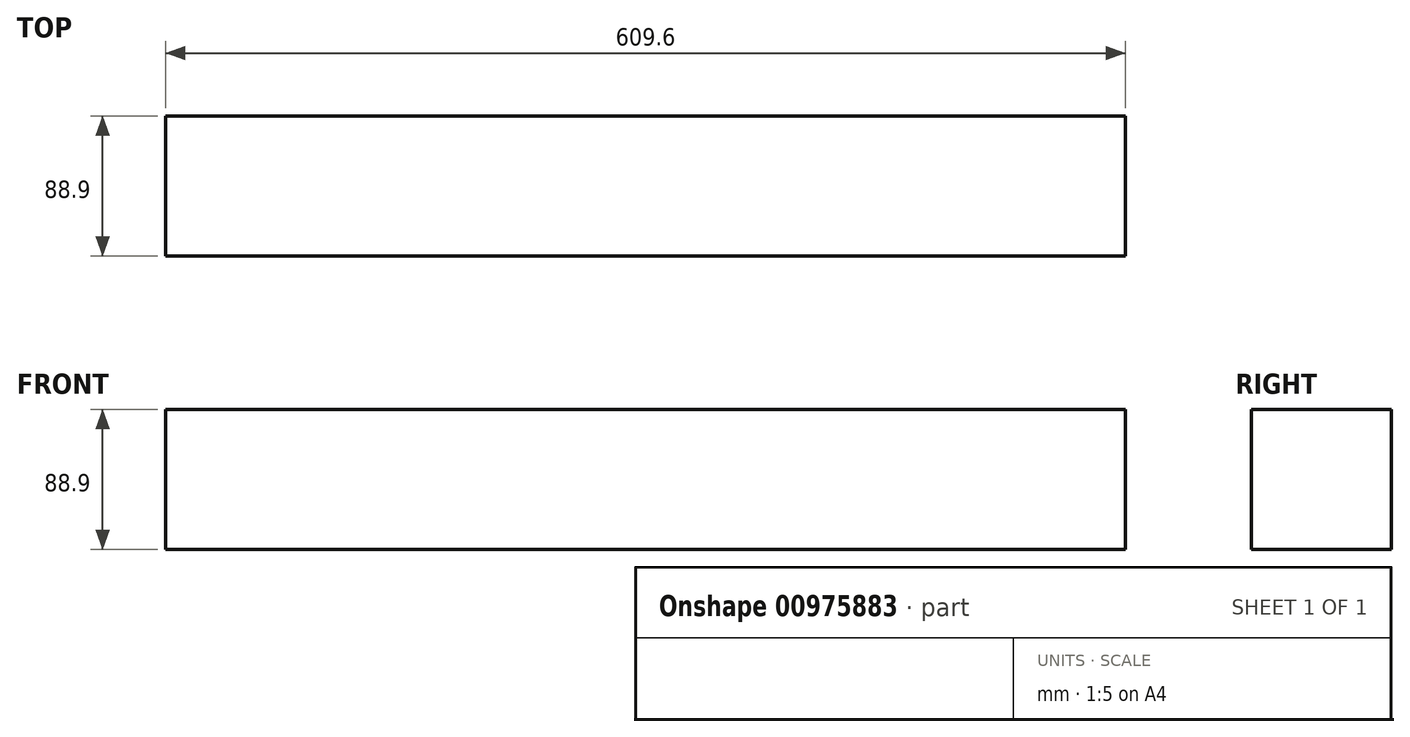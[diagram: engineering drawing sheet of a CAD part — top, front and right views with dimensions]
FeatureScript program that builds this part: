
annotation { "Feature Type Name" : "Feature", "Feature Type Description" : "" }
export const myFeature = defineFeature(function(context is Context, id is Id, definition is map)
    precondition{}
    {
        {
            var Q0;
            Q0=qCreatedBy(makeId("Right.planeOp"),FACE);
            var sketch = newSketch(context, id + "F0", { "sketchPlane" : qUnion([Q0])});
            skLineSegment(sketch, "E0.bottom", {"start": v(0, 0) * mm, "end": v(0, 0) * mm});
            skLineSegment(sketch, "E0.top", {"start": v(0, 0) * mm, "end": v(0, 0) * mm});
            skLineSegment(sketch, "E0.left", {"start": v(0, 0) * mm, "end": v(0, 0) * mm});
            skLineSegment(sketch, "E0.right", {"start": v(0, 0) * mm, "end": v(0, 0) * mm});
            skPoint(sketch, "E0.middle", {"position": v(0, 0) * mm});
            skLineSegment(sketch, "E1.bottom", {"start": v(44.45, 44.45) * mm, "end": v(-44.45, 44.45) * mm});
            skLineSegment(sketch, "E1.top", {"start": v(44.45, -44.45) * mm, "end": v(-44.45, -44.45) * mm});
            skLineSegment(sketch, "E1.left", {"start": v(44.45, 44.45) * mm, "end": v(44.45, -44.45) * mm});
            skLineSegment(sketch, "E1.right", {"start": v(-44.45, 44.45) * mm, "end": v(-44.45, -44.45) * mm});
            skSolve(sketch);
        }
        {
            var Q0;
            Q0=qSketchRegion(id+"F0",true);
            extrude(context, id + "F1", {"entities" : qUnion([Q0]), "depth" : 609.6 * mm, "offsetDistance" : 25.4 * mm});
        }
    });
